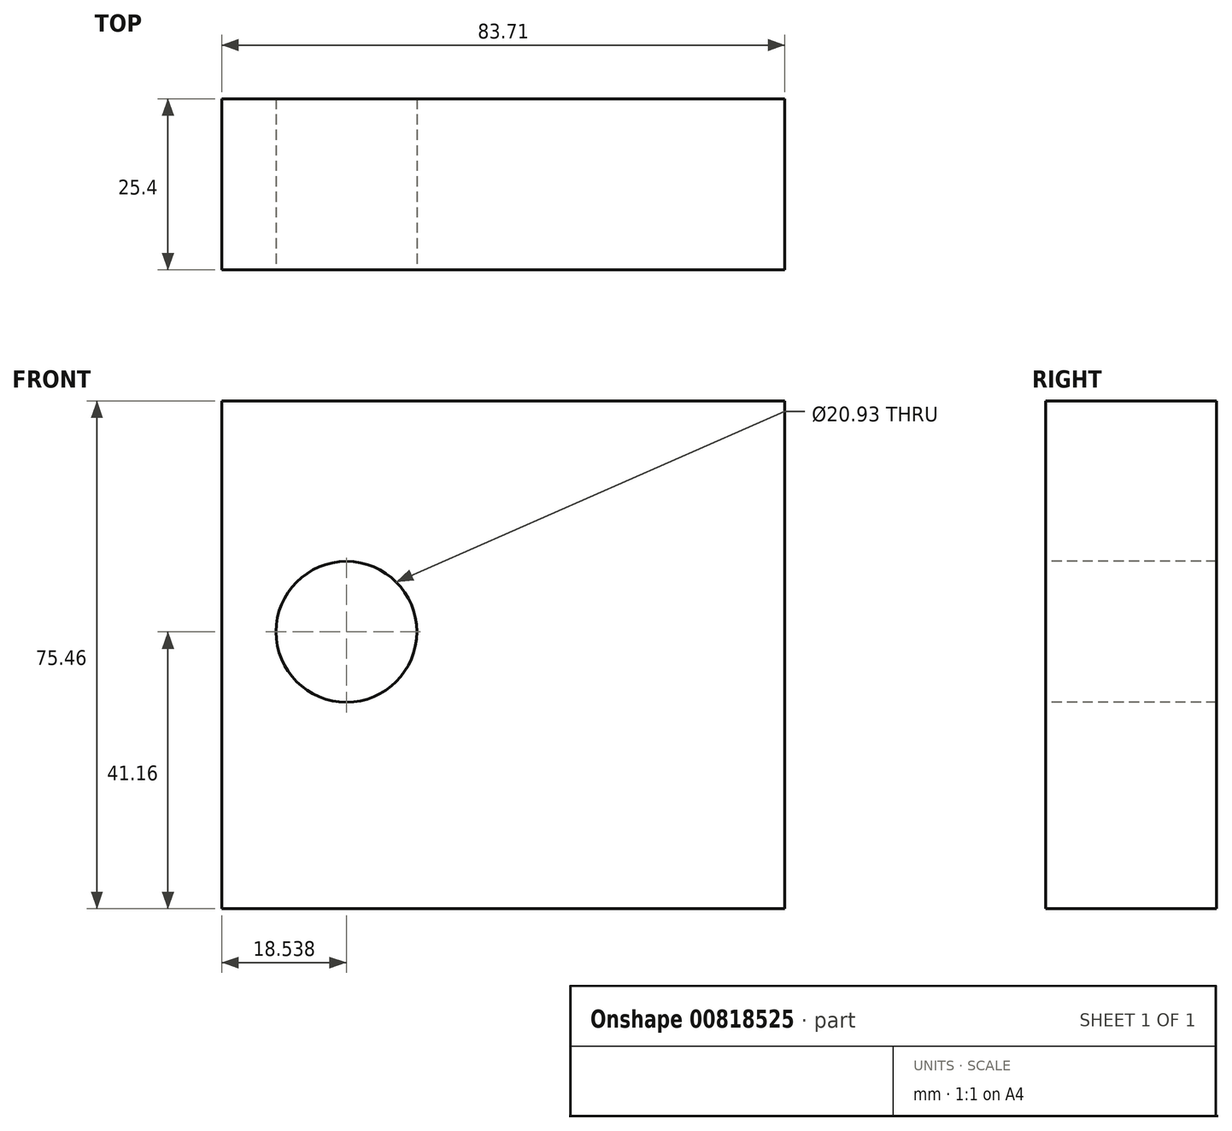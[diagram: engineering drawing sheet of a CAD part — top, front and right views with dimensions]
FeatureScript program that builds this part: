
annotation { "Feature Type Name" : "Feature", "Feature Type Description" : "" }
export const myFeature = defineFeature(function(context is Context, id is Id, definition is map)
    precondition{}
    {
        {
            var Q0;
            Q0=qCreatedBy(makeId("Front.planeOp"),FACE);
            var sketch = newSketch(context, id + "F0", { "sketchPlane" : qUnion([Q0])});
            skLineSegment(sketch, "E0.bottom", {"start": v(-51.45, 49.66) * mm, "end": v(32.26, 49.66) * mm});
            skLineSegment(sketch, "E0.top", {"start": v(-51.45, -25.8) * mm, "end": v(32.26, -25.8) * mm});
            skLineSegment(sketch, "E0.left", {"start": v(-51.45, 49.66) * mm, "end": v(-51.45, -25.8) * mm});
            skLineSegment(sketch, "E0.right", {"start": v(32.26, 49.66) * mm, "end": v(32.26, -25.8) * mm});
            skSolve(sketch);
        }
        {
            var Q0;
            Q0=makeQuery(id+"F0.imprint","IMPRINT",FACE,{"disambiguationData":[TD([[makeQuery(id+"F0.imprint","IMPRINT",EDGE,{"derivedFrom":sQuery(id+"F0.wireOp",EDGE,"E0.bottom")}),-1.0]])]});
            extrude(context, id + "F1", {"entities" : qUnion([Q0]), "depth" : 25.4 * mm, "offsetDistance" : 25.4 * mm});
        }
        {
            var Q0;
            Q0=makeQuery(id+"F1.opExtrude","CAP_FACE",FACE,{"disambiguationData":[OSD([sQuery(id+"F0.wireOp",EDGE,"E0.bottom"),sQuery(id+"F0.wireOp",EDGE,"E0.top"),sQuery(id+"F0.wireOp",EDGE,"E0.left"),sQuery(id+"F0.wireOp",EDGE,"E0.right")])],"isStart":false});
            var sketch = newSketch(context, id + "F2", { "sketchPlane" : qUnion([Q0])});
            skCircle(sketch, "E1", {"center": v(-32.91, 15.36) * mm, "radius": 10.46 * mm});
            skSolve(sketch);
        }
        {
            var Q0;
            Q0 = qSketchRegion(id + "F2", true);
            extrude(context, id + "F3", {"entities" : qUnion([Q0]), "operationType" : NewBodyOperationType.REMOVE, "endBound" : BoundingType.UP_TO_NEXT, "oppositeDirection" : true, "depth" : 25.4 * mm, "offsetDistance" : 25.4 * mm});
        }
    });
